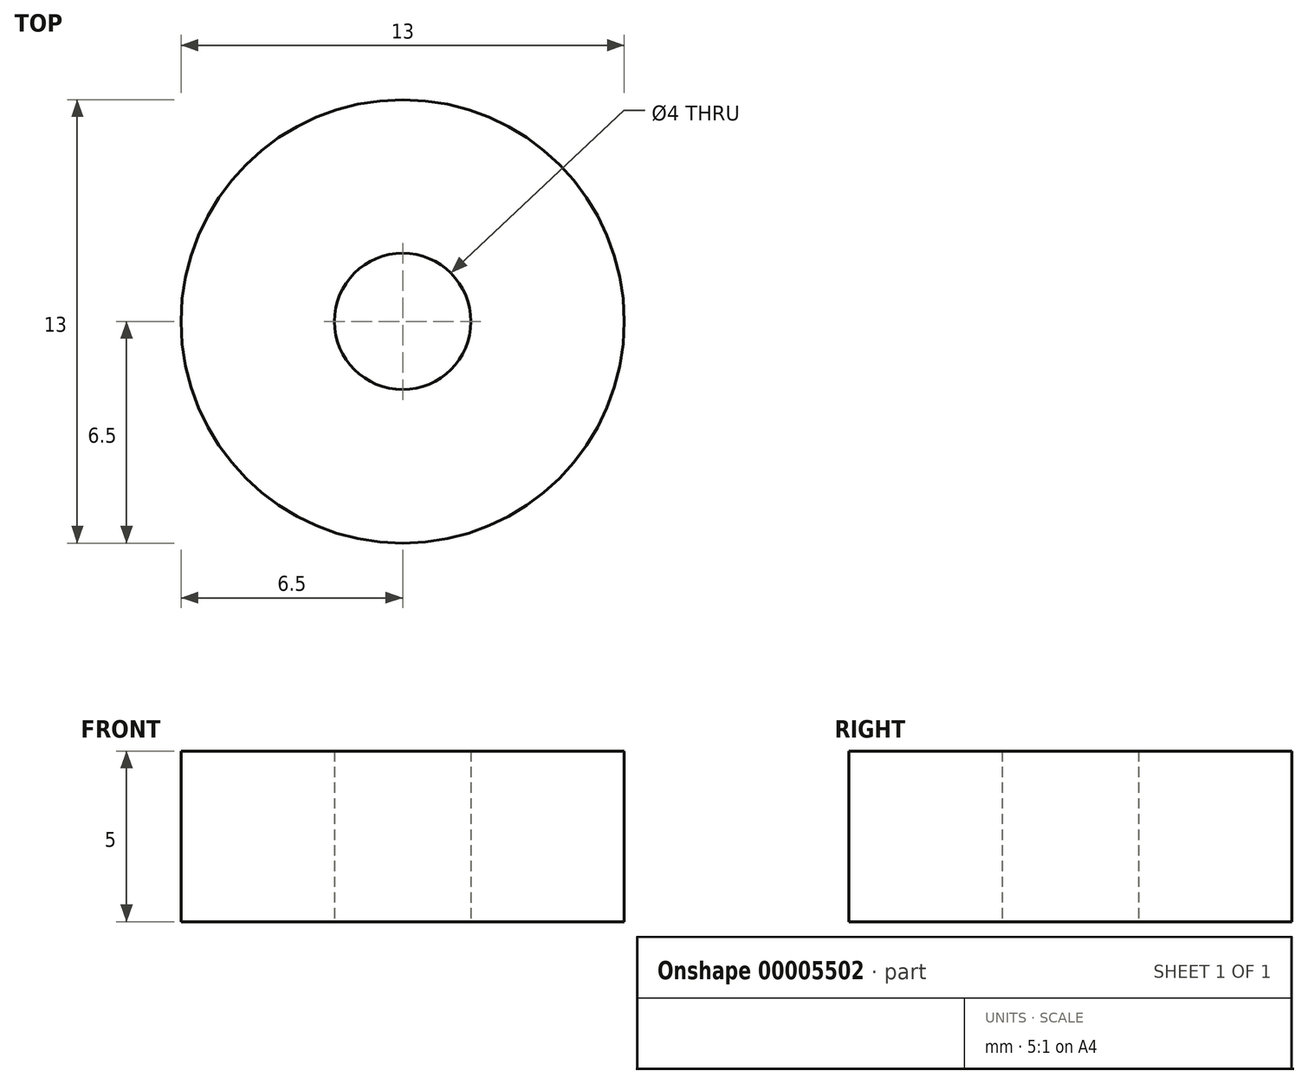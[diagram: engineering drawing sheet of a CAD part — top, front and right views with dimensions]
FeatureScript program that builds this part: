
annotation { "Feature Type Name" : "Feature", "Feature Type Description" : "" }
export const myFeature = defineFeature(function(context is Context, id is Id, definition is map)
    precondition{}
    {
        {
            var Q0;
            Q0=qCreatedBy(makeId("Top.planeOp"),FACE);
            var sketch = newSketch(context, id + "F0", { "sketchPlane" : qUnion([Q0])});
            skCircle(sketch, "E0", {"center": v(0, 0) * mm, "radius": 2 * mm});
            skCircle(sketch, "E1", {"center": v(0, 0) * mm, "radius": 6.5 * mm});
            skSolve(sketch);
        }
        {
            var Q0;
            Q0 = qSketchRegion(id + "F0", true);
            extrude(context, id + "F1", {"entities" : qUnion([Q0]), "depth" : 5 * mm});
        }
    });
